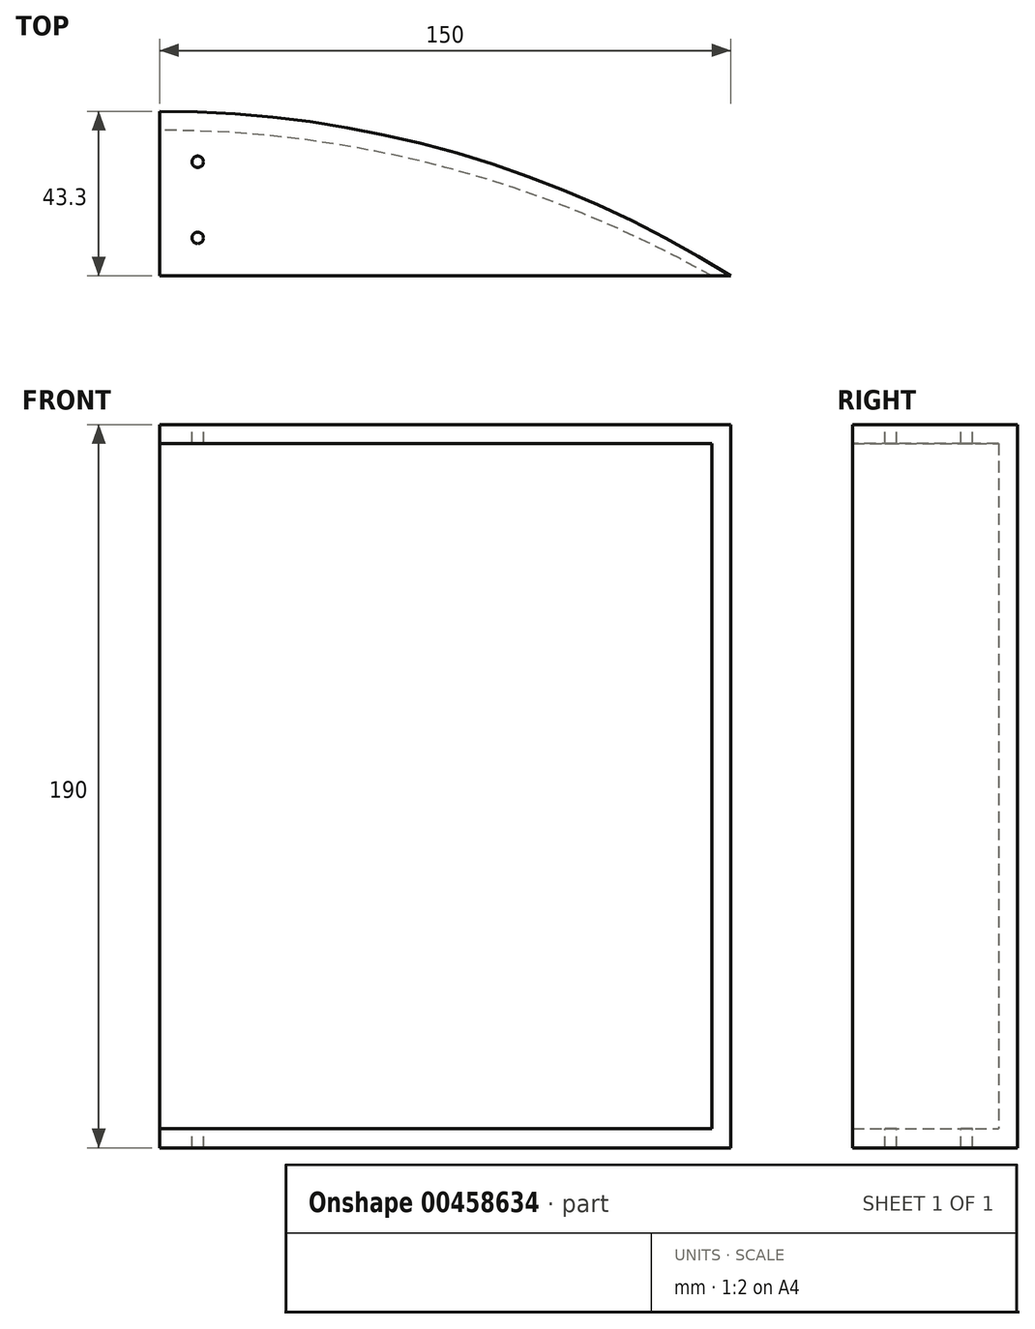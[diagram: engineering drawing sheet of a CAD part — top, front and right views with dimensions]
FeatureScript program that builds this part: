
annotation { "Feature Type Name" : "Feature", "Feature Type Description" : "" }
export const myFeature = defineFeature(function(context is Context, id is Id, definition is map)
    precondition{}
    {
        {
            var Q0;
            Q0=qCreatedBy(makeId("Top.planeOp"),FACE);
            var sketch = newSketch(context, id + "F0", { "sketchPlane" : qUnion([Q0])});
            skLineSegment(sketch, "E0", {"start": v(0, 0) * mm, "end": v(75, 0) * mm});
            skLineSegment(sketch, "E1", {"start": v(0, 0) * mm, "end": v(-75, 0) * mm});
            skLineSegment(sketch, "E2", {"start": v(-75, 0) * mm, "end": v(-75, 43.3) * mm});
            skArc(sketch, "E3", {"start": v(75, 0) * mm, "mid": v(3.06, 32.26) * mm, "end": v(-75, 43.3) * mm});
            skSolve(sketch);
        }
        {
            var Q0;
            Q0=makeQuery(id+"F0.imprint","IMPRINT",FACE,{"disambiguationData":[TD([[makeQuery(id+"F0.imprint","IMPRINT",EDGE,{"derivedFrom":sQuery(id+"F0.wireOp",EDGE,"E0")}),1.0]])]});
            extrude(context, id + "F1", {"entities" : qUnion([Q0]), "depth" : 5 * mm});
        }
        {
            var Q0;
            Q0=makeQuery(id+"F1.opExtrude","CAP_FACE",FACE,{"disambiguationData":[OSD([sQuery(id+"F0.wireOp",EDGE,"E0"),sQuery(id+"F0.wireOp",EDGE,"E1"),sQuery(id+"F0.wireOp",EDGE,"E2"),sQuery(id+"F0.wireOp",EDGE,"E3")])],"isStart":false});
            var sketch = newSketch(context, id + "F2", { "sketchPlane" : qUnion([Q0])});
            skLineSegment(sketch, "E4", {"start": v(-75, 43.3) * mm, "end": v(-75, 38.3) * mm});
            skLineSegment(sketch, "E5", {"start": v(75, 0) * mm, "end": v(70, 0) * mm});
            skArc(sketch, "E6", {"start": v(70, 0) * mm, "mid": v(-0.01, 28.56) * mm, "end": v(-75, 38.3) * mm});
            skSolve(sketch);
        }
        {
            var Q0;
            Q0=makeQuery(id+"F2.imprint","IMPRINT",FACE,{"disambiguationData":[TD([[makeQuery(id+"F2.imprint","IMPRINT",EDGE,{"derivedFrom":sQuery(id+"F2.wireOp",EDGE,"E4")}),-1.0]])]});
            extrude(context, id + "F3", {"entities" : qUnion([Q0]), "operationType" : NewBodyOperationType.ADD, "depth" : 180 * mm});
        }
        {
            var Q0;
            Q0=makeQuery(id+"F3.opExtrude","CAP_FACE",FACE,{"disambiguationData":[OSD([sQuery(id+"F0.wireOp",EDGE,"E3"),sQuery(id+"F2.wireOp",EDGE,"E4"),sQuery(id+"F2.wireOp",EDGE,"E5"),sQuery(id+"F2.wireOp",EDGE,"E6")])],"isStart":false});
            var sketch = newSketch(context, id + "F4", { "sketchPlane" : qUnion([Q0])});
            skLineSegment(sketch, "E7", {"start": v(-75, 38.3) * mm, "end": v(-75, 0) * mm});
            skLineSegment(sketch, "E8", {"start": v(-75, 0) * mm, "end": v(70, 0) * mm});
            skSolve(sketch);
        }
        {
            var Q0;
            Q0=makeQuery(id+"F4.imprint","IMPRINT",FACE,{"disambiguationData":[TD([[makeQuery(id+"F4.imprint","IMPRINT",EDGE,{"derivedFrom":sQuery(id+"F4.wireOp",EDGE,"E7")}),1.0]])]});
            var Q1;
            Q1=makeQuery(id+"F4.imprint","IMPRINT",FACE,{"disambiguationData":[TD([[makeQuery(id+"F4.imprint","IMPRINT",EDGE,{"derivedFrom":makeQuery(id+"F3.opExtrude","CAP_EDGE",EDGE,{"disambiguationData":[OSD([sQuery(id+"F2.wireOp",EDGE,"E4")])],"isStart":false})}),-1.0]])]});
            extrude(context, id + "F5", {"entities" : qUnion([Q0, Q1]), "operationType" : NewBodyOperationType.ADD, "depth" : 5 * mm});
        }
        {
            var Q0;
            Q0=makeQuery(id+"F5.opExtrude","CAP_FACE",FACE,{"disambiguationData":[OSD([sQuery(id+"F0.wireOp",EDGE,"E3"),sQuery(id+"F2.wireOp",EDGE,"E4"),sQuery(id+"F2.wireOp",EDGE,"E5"),sQuery(id+"F4.wireOp",EDGE,"E7"),sQuery(id+"F4.wireOp",EDGE,"E8")])],"isStart":false});
            var sketch = newSketch(context, id + "F6", { "sketchPlane" : qUnion([Q0])});
            skLineSegment(sketch, "E9", {"start": v(-65, 0) * mm, "end": v(-65, 10) * mm});
            skLineSegment(sketch, "E10", {"start": v(-65, 10) * mm, "end": v(-75, 10) * mm});
            skLineSegment(sketch, "E11", {"start": v(-65, 10) * mm, "end": v(-65, 30) * mm});
            skLineSegment(sketch, "E12", {"start": v(-65, 30) * mm, "end": v(-75, 30) * mm});
            skSolve(sketch);
        }
        {
            var Q0;
            Q0=sQuery(id+"F6.wireOp",VERTEX,"E12.start");
            var Q1;
            Q1=sQuery(id+"F6.wireOp",VERTEX,"E11.start");
            var Q2;
            Q2=makeQuery(id+"F1.opExtrude","SWEPT_BODY",BODY,{"disambiguationData":[OSD([sQuery(id+"F0.wireOp",EDGE,"E0"),sQuery(id+"F0.wireOp",EDGE,"E1"),sQuery(id+"F0.wireOp",EDGE,"E2"),sQuery(id+"F0.wireOp",EDGE,"E3")])]});
            hole(context, id + "F7", {"style" : HoleStyle.SIMPLE, "endStyle" : HoleEndStyle.BLIND, "holeDiameter" : 3 * mm, "holeDepth" : 200 * mm, "isTappedThrough" : true, "tappedDepth" : 12 * mm, "tapClearance" : 3, "locations" : qUnion([Q0, Q1]), "scope" : qUnion([Q2])});
        }
    });
